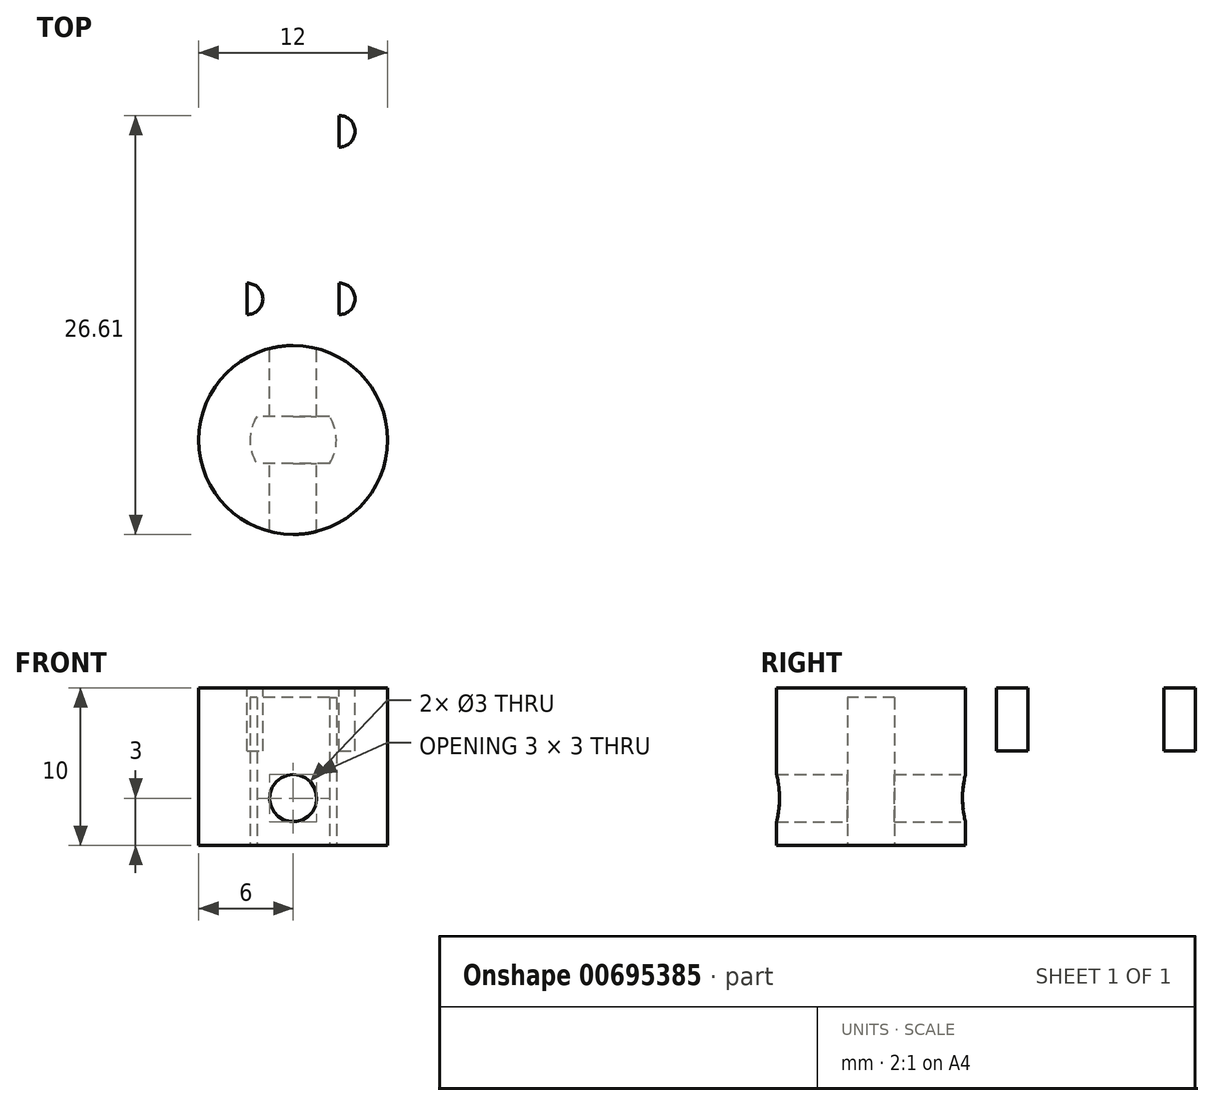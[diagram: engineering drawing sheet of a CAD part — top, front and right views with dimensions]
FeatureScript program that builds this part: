
annotation { "Feature Type Name" : "Feature", "Feature Type Description" : "" }
export const myFeature = defineFeature(function(context is Context, id is Id, definition is map)
    precondition{}
    {
        {
            var Q0;
            Q0=qCreatedBy(makeId("Top.planeOp"),FACE);
            var sketch = newSketch(context, id + "F0", { "sketchPlane" : qUnion([Q0])});
            skCircle(sketch, "E0", {"center": v(0, 0) * mm, "radius": 30 * mm});
            skCircle(sketch, "E1", {"center": v(0, 0) * mm, "radius": 6 * mm});
            skSolve(sketch);
        }
        {
            var Q0;
            Q0 = qSketchRegion(id + "F0", true);
            var Q1;
            Q1=makeQuery(id+"F0.imprint","IMPRINT",FACE,{"disambiguationData":[TD([[makeQuery(id+"F0.imprint","IMPRINT",EDGE,{"derivedFrom":sQuery(id+"F0.wireOp",EDGE,"E1")}),1.0]])]});
            extrude(context, id + "F1", {"entities" : qUnion([Q0, Q1]), "depth" : 4 * mm, "offsetDistance" : 25 * mm});
        }
        {
            var Q0;
            Q0=makeQuery(id+"F0.imprint","IMPRINT",FACE,{"disambiguationData":[TD([[makeQuery(id+"F0.imprint","IMPRINT",EDGE,{"derivedFrom":sQuery(id+"F0.wireOp",EDGE,"E1")}),1.0]])]});
            extrude(context, id + "F2", {"entities" : qUnion([Q0]), "operationType" : NewBodyOperationType.ADD, "oppositeDirection" : true, "depth" : 6 * mm, "offsetDistance" : 25 * mm});
        }
        {
            var Q0;
            Q0=qCreatedBy(makeId("Front.planeOp"),FACE);
            var sketch = newSketch(context, id + "F3", { "sketchPlane" : qUnion([Q0])});
            skCircle(sketch, "E2", {"center": v(0, -3) * mm, "radius": 1.5 * mm});
            skSolve(sketch);
        }
        {
            var Q0;
            Q0 = qSketchRegion(id + "F3", true);
            extrude(context, id + "F4", {"entities" : qUnion([Q0]), "operationType" : NewBodyOperationType.REMOVE, "endBound" : BoundingType.SYMMETRIC, "depth" : 26 * mm, "offsetDistance" : 25 * mm});
        }
        {
            var Q0;
            Q0=makeQuery(id+"F2.opExtrude","CAP_FACE",FACE,{"disambiguationData":[OSD([sQuery(id+"F0.wireOp",EDGE,"E1")])],"isStart":false});
            var sketch = newSketch(context, id + "F5", { "sketchPlane" : qUnion([Q0])});
            skLineSegment(sketch, "E3.bottom", {"start": v(2.3, 1.5) * mm, "end": v(-2.3, 1.5) * mm});
            skLineSegment(sketch, "E3.top", {"start": v(2.3, -1.5) * mm, "end": v(-2.3, -1.5) * mm});
            skLineSegment(sketch, "E3.left", {"start": v(2.3, 1.5) * mm, "end": v(2.3, -1.5) * mm});
            skLineSegment(sketch, "E3.right", {"start": v(-2.3, 1.5) * mm, "end": v(-2.3, -1.5) * mm});
            skPoint(sketch, "E3.middle", {"position": v(0, 0) * mm});
            skArc(sketch, "E4", {"start": v(2.3, -1.5) * mm, "mid": v(2.75, 0) * mm, "end": v(2.3, 1.5) * mm});
            skArc(sketch, "E5", {"start": v(-2.3, 1.5) * mm, "mid": v(-2.75, 0) * mm, "end": v(-2.3, -1.5) * mm});
            skSolve(sketch);
        }
        {
            var Q0;
            Q0=makeQuery(id+"F5.imprint","IMPRINT",FACE,{"disambiguationData":[TD([[makeQuery(id+"F5.imprint","IMPRINT",EDGE,{"derivedFrom":sQuery(id+"F5.wireOp",EDGE,"E3.left")}),1.0]])]});
            var Q1;
            Q1=makeQuery(id+"F5.imprint","IMPRINT",FACE,{"disambiguationData":[TD([[makeQuery(id+"F5.imprint","IMPRINT",EDGE,{"derivedFrom":sQuery(id+"F5.wireOp",EDGE,"E3.bottom")}),1.0]])]});
            var Q2;
            Q2=makeQuery(id+"F5.imprint","IMPRINT",FACE,{"disambiguationData":[TD([[makeQuery(id+"F5.imprint","IMPRINT",EDGE,{"derivedFrom":sQuery(id+"F5.wireOp",EDGE,"E3.right")}),-1.0]])]});
            extrude(context, id + "F6", {"entities" : qUnion([Q0, Q1, Q2]), "operationType" : NewBodyOperationType.REMOVE, "oppositeDirection" : true, "depth" : 9.4 * mm, "offsetDistance" : 25 * mm});
        }
        {
            var Q0;
            Q0=qCreatedBy(makeId("Front.planeOp"),FACE);
            var sketch = newSketch(context, id + "F7", { "sketchPlane" : qUnion([Q0])});
            skLineSegment(sketch, "E6", {"start": v(-30, -0.04) * mm, "end": v(-30, 4) * mm});
            skLineSegment(sketch, "E7", {"start": v(-30, 0) * mm, "end": v(-30, 3.96) * mm});
            skLineSegment(sketch, "E8", {"start": v(-30, 0.55) * mm, "end": v(-28.59, 1.96) * mm});
            skLineSegment(sketch, "E9", {"start": v(-28.59, 1.96) * mm, "end": v(-30, 3.38) * mm});
            skSolve(sketch);
        }
        {
            var Q0;
            Q0=qCreatedBy(makeId("Front.planeOp"),FACE);
            var sketch = newSketch(context, id + "F8", { "sketchPlane" : qUnion([Q0])});
            skLineSegment(sketch, "E10", {"start": v(0, -15.8) * mm, "end": v(0, 8.44) * mm, "construction": true});
            skSolve(sketch);
        }
        {
            var Q0;
            Q0 = qSketchRegion(id + "F7", true);
            var Q1;
            Q1 = qConstructionFilter(qBodyType(qCreatedBy(id + "F7" ,EDGE), BodyType.WIRE), ConstructionObject.NO);
            var Q2;
            Q2=sQuery(id+"F8.wireOp",EDGE,"E10");
            revolve(context, id + "F9", {"operationType" : NewBodyOperationType.REMOVE, "surfaceOperationType" : NewSurfaceOperationType.NEW, "entities" : qUnion([Q0]), "surfaceEntities" : qUnion([Q1]), "axis" : qUnion([Q2]), "revolveType" : RevolveType.FULL, "oppositeDirection" : true});
        }
        {
            var Q0;
            Q0=makeQuery(id+"F0.imprint","IMPRINT",FACE,{"disambiguationData":[TD([[makeQuery(id+"F0.imprint","IMPRINT",EDGE,{"derivedFrom":sQuery(id+"F0.wireOp",EDGE,"E0")}),1.0]])]});
            var sketch = newSketch(context, id + "F10", { "sketchPlane" : qUnion([Q0])});
            skLineSegment(sketch, "E11", {"start": v(0, 0) * mm, "end": v(0, 23.18) * mm, "construction": true});
            skLineSegment(sketch, "E12.bottom", {"start": v(5.66, 19.6) * mm, "end": v(-5.66, 19.6) * mm});
            skLineSegment(sketch, "E12.top", {"start": v(5.66, 8.96) * mm, "end": v(-5.66, 8.96) * mm});
            skLineSegment(sketch, "E12.left", {"start": v(5.66, 19.6) * mm, "end": v(5.66, 8.96) * mm});
            skLineSegment(sketch, "E12.right", {"start": v(-5.66, 19.6) * mm, "end": v(-5.66, 8.96) * mm});
            skPoint(sketch, "E12.middle", {"position": v(0, 14.28) * mm});
            skLineSegment(sketch, "E13.bottom", {"start": v(2.93, 21.4) * mm, "end": v(-2.93, 21.4) * mm});
            skLineSegment(sketch, "E13.top", {"start": v(2.93, 7.16) * mm, "end": v(-2.93, 7.16) * mm});
            skLineSegment(sketch, "E13.left", {"start": v(2.93, 21.4) * mm, "end": v(2.93, 7.16) * mm});
            skLineSegment(sketch, "E13.right", {"start": v(-2.93, 21.4) * mm, "end": v(-2.93, 7.16) * mm});
            skCircle(sketch, "E14", {"center": v(2.93, 19.6) * mm, "radius": 1 * mm});
            skCircle(sketch, "E15", {"center": v(-2.93, 19.6) * mm, "radius": 1 * mm});
            skCircle(sketch, "E16", {"center": v(2.93, 8.96) * mm, "radius": 1 * mm});
            skCircle(sketch, "E17", {"center": v(-2.93, 8.96) * mm, "radius": 1 * mm});
            skSolve(sketch);
        }
        {
            var Q0;
            {var subQ5=sQuery(id+"F10.wireOp",EDGE,"E12.left");Q0=makeQuery(id+"F10.imprint","IMPRINT",FACE,{"disambiguationData":[TD([[makeQuery(id+"F10.imprint","IMPRINT",EDGE,{"derivedFrom":subQ5}),-1.0]])]});}
            var Q1;
            {var subQ0=sQuery(id+"F10.wireOp",EDGE,"E12.right");Q1=makeQuery(id+"F10.imprint","IMPRINT",FACE,{"disambiguationData":[TD([[makeQuery(id+"F10.imprint","IMPRINT",EDGE,{"derivedFrom":subQ0}),1.0]])]});}
            var Q2;
            {var subQ0=sQuery(id+"F10.wireOp",EDGE,"E14");var subQ1=sQuery(id+"F10.wireOp",EDGE,"E12.bottom");var subQ2=makeQuery(id+"F10.imprint","INTERSECT",VERTEX,{"disambiguationData":[OD(0.0)],"derivedFrom":[subQ1,subQ0]});Q2=makeQuery(id+"F10.imprint","IMPRINT",FACE,{"disambiguationData":[TD([[makeQuery(id+"F10.imprint","IMPRINT",EDGE,{"disambiguationData":[TD([[subQ2,-1.0]])],"derivedFrom":subQ1}),1.0]])]});}
            var Q3;
            {var subQ0=sQuery(id+"F10.wireOp",EDGE,"E13.left");var subQ1=sQuery(id+"F10.wireOp",EDGE,"E12.bottom");var subQ2=makeQuery(id+"F10.imprint","INTERSECT",VERTEX,{"derivedFrom":[subQ1,subQ0]});Q3=makeQuery(id+"F10.imprint","IMPRINT",FACE,{"disambiguationData":[TD([[makeQuery(id+"F10.imprint","IMPRINT",EDGE,{"disambiguationData":[TD([[subQ2,-1.0]])],"derivedFrom":subQ1}),1.0]])]});}
            var Q4;
            {var subQ0=sQuery(id+"F10.wireOp",EDGE,"E13.right");var subQ1=sQuery(id+"F10.wireOp",EDGE,"E12.bottom");var subQ2=makeQuery(id+"F10.imprint","INTERSECT",VERTEX,{"derivedFrom":[subQ1,subQ0]});Q4=makeQuery(id+"F10.imprint","IMPRINT",FACE,{"disambiguationData":[TD([[makeQuery(id+"F10.imprint","IMPRINT",EDGE,{"disambiguationData":[TD([[subQ2,-1.0]])],"derivedFrom":subQ1}),1.0]])]});}
            var Q5;
            {var subQ0=sQuery(id+"F10.wireOp",EDGE,"E16");var subQ1=sQuery(id+"F10.wireOp",EDGE,"E12.top");var subQ2=makeQuery(id+"F10.imprint","INTERSECT",VERTEX,{"disambiguationData":[OD(0.0)],"derivedFrom":[subQ1,subQ0]});Q5=makeQuery(id+"F10.imprint","IMPRINT",FACE,{"disambiguationData":[TD([[makeQuery(id+"F10.imprint","IMPRINT",EDGE,{"disambiguationData":[TD([[subQ2,-1.0]])],"derivedFrom":subQ1}),-1.0]])]});}
            var Q6;
            {var subQ0=sQuery(id+"F10.wireOp",EDGE,"E15");var subQ1=sQuery(id+"F10.wireOp",EDGE,"E12.bottom");var subQ2=makeQuery(id+"F10.imprint","INTERSECT",VERTEX,{"disambiguationData":[OD(0.0)],"derivedFrom":[subQ1,subQ0]});Q6=makeQuery(id+"F10.imprint","IMPRINT",FACE,{"disambiguationData":[TD([[makeQuery(id+"F10.imprint","IMPRINT",EDGE,{"disambiguationData":[TD([[subQ2,-1.0]])],"derivedFrom":subQ1}),1.0]])]});}
            var Q7;
            {var subQ0=sQuery(id+"F10.wireOp",EDGE,"E13.right");var subQ1=sQuery(id+"F10.wireOp",EDGE,"E12.top");var subQ2=makeQuery(id+"F10.imprint","INTERSECT",VERTEX,{"derivedFrom":[subQ1,subQ0]});Q7=makeQuery(id+"F10.imprint","IMPRINT",FACE,{"disambiguationData":[TD([[makeQuery(id+"F10.imprint","IMPRINT",EDGE,{"disambiguationData":[TD([[subQ2,-1.0]])],"derivedFrom":subQ1}),-1.0]])]});}
            var Q8;
            {var subQ0=sQuery(id+"F10.wireOp",EDGE,"E13.left");var subQ1=sQuery(id+"F10.wireOp",EDGE,"E12.top");var subQ2=makeQuery(id+"F10.imprint","INTERSECT",VERTEX,{"derivedFrom":[subQ1,subQ0]});Q8=makeQuery(id+"F10.imprint","IMPRINT",FACE,{"disambiguationData":[TD([[makeQuery(id+"F10.imprint","IMPRINT",EDGE,{"disambiguationData":[TD([[subQ2,-1.0]])],"derivedFrom":subQ1}),-1.0]])]});}
            var Q9;
            {var subQ0=sQuery(id+"F10.wireOp",EDGE,"E17");var subQ1=sQuery(id+"F10.wireOp",EDGE,"E12.top");var subQ2=makeQuery(id+"F10.imprint","INTERSECT",VERTEX,{"disambiguationData":[OD(0.0)],"derivedFrom":[subQ1,subQ0]});Q9=makeQuery(id+"F10.imprint","IMPRINT",FACE,{"disambiguationData":[TD([[makeQuery(id+"F10.imprint","IMPRINT",EDGE,{"disambiguationData":[TD([[subQ2,-1.0]])],"derivedFrom":subQ1}),-1.0]])]});}
            var Q10;
            {var subQ0=sQuery(id+"F10.wireOp",EDGE,"E14");var subQ1=sQuery(id+"F10.wireOp",EDGE,"E12.bottom");var subQ2=makeQuery(id+"F10.imprint","INTERSECT",VERTEX,{"disambiguationData":[OD(0.0)],"derivedFrom":[subQ1,subQ0]});Q10=makeQuery(id+"F10.imprint","IMPRINT",FACE,{"disambiguationData":[TD([[makeQuery(id+"F10.imprint","IMPRINT",EDGE,{"disambiguationData":[TD([[subQ2,-1.0]])],"derivedFrom":subQ1}),-1.0]])]});}
            var Q11;
            {var subQ0=sQuery(id+"F10.wireOp",EDGE,"E13.left");var subQ1=sQuery(id+"F10.wireOp",EDGE,"E12.bottom");var subQ2=makeQuery(id+"F10.imprint","INTERSECT",VERTEX,{"derivedFrom":[subQ1,subQ0]});Q11=makeQuery(id+"F10.imprint","IMPRINT",FACE,{"disambiguationData":[TD([[makeQuery(id+"F10.imprint","IMPRINT",EDGE,{"disambiguationData":[TD([[subQ2,-1.0]])],"derivedFrom":subQ1}),-1.0]])]});}
            var Q12;
            {var subQ0=sQuery(id+"F10.wireOp",EDGE,"E15");var subQ1=sQuery(id+"F10.wireOp",EDGE,"E12.bottom");var subQ2=makeQuery(id+"F10.imprint","INTERSECT",VERTEX,{"disambiguationData":[OD(0.0)],"derivedFrom":[subQ1,subQ0]});Q12=makeQuery(id+"F10.imprint","IMPRINT",FACE,{"disambiguationData":[TD([[makeQuery(id+"F10.imprint","IMPRINT",EDGE,{"disambiguationData":[TD([[subQ2,-1.0]])],"derivedFrom":subQ1}),-1.0]])]});}
            var Q13;
            {var subQ0=sQuery(id+"F10.wireOp",EDGE,"E13.right");var subQ1=sQuery(id+"F10.wireOp",EDGE,"E12.bottom");var subQ2=makeQuery(id+"F10.imprint","INTERSECT",VERTEX,{"derivedFrom":[subQ1,subQ0]});Q13=makeQuery(id+"F10.imprint","IMPRINT",FACE,{"disambiguationData":[TD([[makeQuery(id+"F10.imprint","IMPRINT",EDGE,{"disambiguationData":[TD([[subQ2,-1.0]])],"derivedFrom":subQ1}),-1.0]])]});}
            var Q14;
            {var subQ0=sQuery(id+"F10.wireOp",EDGE,"E17");var subQ1=sQuery(id+"F10.wireOp",EDGE,"E12.top");var subQ2=makeQuery(id+"F10.imprint","INTERSECT",VERTEX,{"disambiguationData":[OD(0.0)],"derivedFrom":[subQ1,subQ0]});Q14=makeQuery(id+"F10.imprint","IMPRINT",FACE,{"disambiguationData":[TD([[makeQuery(id+"F10.imprint","IMPRINT",EDGE,{"disambiguationData":[TD([[subQ2,-1.0]])],"derivedFrom":subQ1}),1.0]])]});}
            var Q15;
            {var subQ0=sQuery(id+"F10.wireOp",EDGE,"E13.left");var subQ1=sQuery(id+"F10.wireOp",EDGE,"E12.top");var subQ2=makeQuery(id+"F10.imprint","INTERSECT",VERTEX,{"derivedFrom":[subQ1,subQ0]});Q15=makeQuery(id+"F10.imprint","IMPRINT",FACE,{"disambiguationData":[TD([[makeQuery(id+"F10.imprint","IMPRINT",EDGE,{"disambiguationData":[TD([[subQ2,-1.0]])],"derivedFrom":subQ1}),1.0]])]});}
            var Q16;
            {var subQ0=sQuery(id+"F10.wireOp",EDGE,"E16");var subQ1=sQuery(id+"F10.wireOp",EDGE,"E12.top");var subQ2=makeQuery(id+"F10.imprint","INTERSECT",VERTEX,{"disambiguationData":[OD(0.0)],"derivedFrom":[subQ1,subQ0]});Q16=makeQuery(id+"F10.imprint","IMPRINT",FACE,{"disambiguationData":[TD([[makeQuery(id+"F10.imprint","IMPRINT",EDGE,{"disambiguationData":[TD([[subQ2,-1.0]])],"derivedFrom":subQ1}),1.0]])]});}
            var Q17;
            {var subQ0=sQuery(id+"F10.wireOp",EDGE,"E13.right");var subQ1=sQuery(id+"F10.wireOp",EDGE,"E12.top");var subQ2=makeQuery(id+"F10.imprint","INTERSECT",VERTEX,{"derivedFrom":[subQ1,subQ0]});Q17=makeQuery(id+"F10.imprint","IMPRINT",FACE,{"disambiguationData":[TD([[makeQuery(id+"F10.imprint","IMPRINT",EDGE,{"disambiguationData":[TD([[subQ2,-1.0]])],"derivedFrom":subQ1}),1.0]])]});}
            extrude(context, id + "F11", {"entities" : qUnion([Q0, Q1, Q2, Q3, Q4, Q5, Q6, Q7, Q8, Q9, Q10, Q11, Q12, Q13, Q14, Q15, Q16, Q17]), "operationType" : NewBodyOperationType.REMOVE, "endBound" : BoundingType.SYMMETRIC, "oppositeDirection" : true, "depth" : 10 * mm, "offsetDistance" : 25 * mm});
        }
        {
            var Q0;
            Q0=qCreatedBy(makeId("Front.planeOp"),FACE);
            var sketch = newSketch(context, id + "F12", { "sketchPlane" : qUnion([Q0])});
            skLineSegment(sketch, "E18", {"start": v(0, -28.6) * mm, "end": v(0, 19.26) * mm});
            skSolve(sketch);
        }
    });
